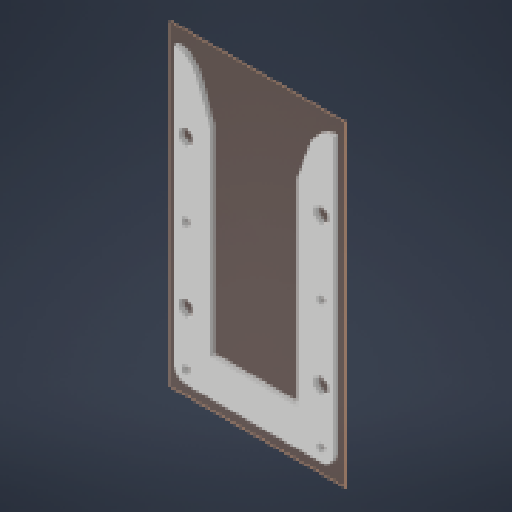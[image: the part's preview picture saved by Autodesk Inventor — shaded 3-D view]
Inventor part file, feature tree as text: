
AUTODESK INVENTOR PART (.ipt)
format: ipt  version: 2023 (Build 270158000, 158)  size: 227,840 bytes
history: native  units: mm
features: other x3, plane x1, extrude x1, sketch x1, reference x1
ambient origin geometry x8: Origin, YZ Plane, XZ Plane, XY Plane, X Axis, Y Axis, Z Axis, Center Point
bodies: Solid1 (feature_tree)
feature tree (7):
  plane  "Work Plane1"
  extrude  "Extrusion1"  Depth=5.0mm
  sketch  "Sketch1"  dims[d0=5.0mm d1=5.0mm d2=5.0mm d3=3.490659mm d5=2.0mm d6=0.0mm]
  reference  "Reference1"
  parser-record x1  (decoder bookkeeping rows leaked as tree rows — omitted from the tree; the rows remain in map.json)
  other  "total.iam"
  other  "middle spacer top:1"
note: 1 file-system path scrubbed to <path> (originals preserved in map.json)
